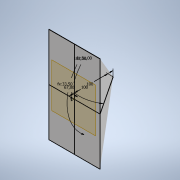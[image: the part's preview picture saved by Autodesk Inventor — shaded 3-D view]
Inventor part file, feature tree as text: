
AUTODESK INVENTOR PART (.ipt)
format: ipt  version: 2022 (Build 260153000, 153)  size: 119,296 bytes
history: native  units: mm
features: sketch x5, other x2, extrude x2, projected_geometry x1
ambient origin geometry x8: Origin, YZ Plane, XZ Plane, XY Plane, X Axis, Y Axis, Z Axis, Center Point
bodies: Body1 (feature_tree)
feature tree (10):
  other  "Твердое тело1"
  sketch  "Эскиз1"
  sketch  "Эскиз2"
  other  "РабПлоскость1"
  sketch  "Эскиз3"
  extrude  "Выдавливание1"  Depth=11.693706mm
  extrude  "Выдавливание2"  Depth=5.846853mm
  sketch  "Эскиз4"
  sketch  "Эскиз5"
  projected_geometry  "Спроецированная петля1"
